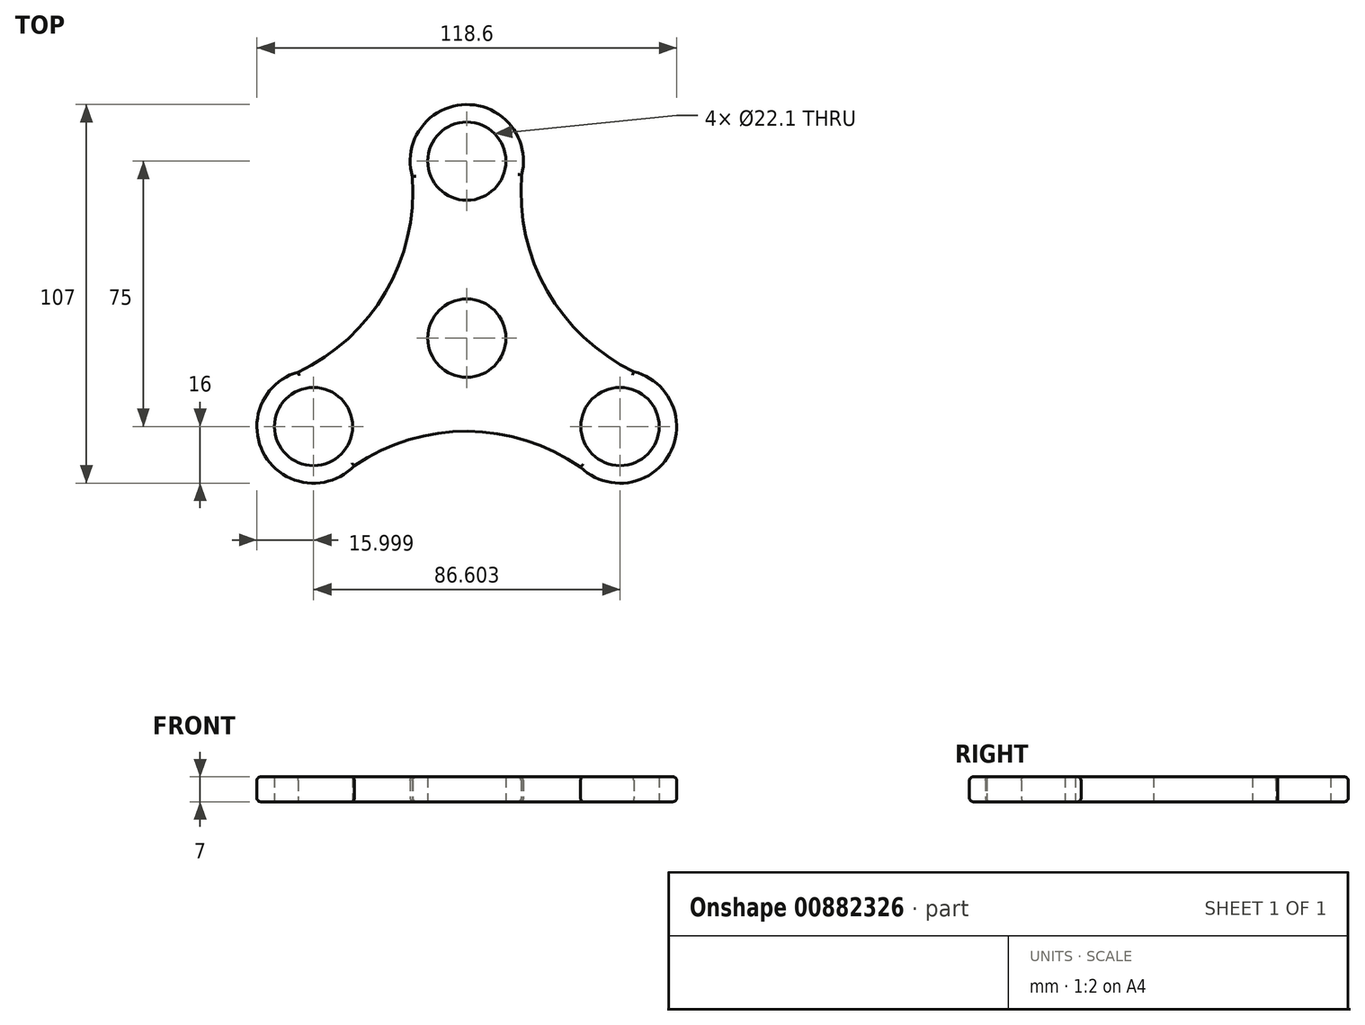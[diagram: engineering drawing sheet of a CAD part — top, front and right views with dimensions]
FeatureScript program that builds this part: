
annotation { "Feature Type Name" : "Feature", "Feature Type Description" : "" }
export const myFeature = defineFeature(function(context is Context, id is Id, definition is map)
    precondition{}
    {
        {
            var Q0;
            Q0=qCreatedBy(makeId("Top.planeOp"),FACE);
            var sketch = newSketch(context, id + "F0", { "sketchPlane" : qUnion([Q0])});
            skCircle(sketch, "E0", {"center": v(0, 0) * mm, "radius": 11.05 * mm});
            skCircle(sketch, "E1", {"center": v(0, 50) * mm, "radius": 11.05 * mm});
            skCircle(sketch, "E2.1.0", {"center": v(43.3, -25) * mm, "radius": 11.05 * mm});
            skCircle(sketch, "E2.2.0", {"center": v(-43.3, -25) * mm, "radius": 11.05 * mm});
            skLineSegment(sketch, "E2.anchor1", {"start": v(0, 0) * mm, "end": v(0, 50) * mm, "construction": true});
            skLineSegment(sketch, "E2.anchor2", {"start": v(0, 0) * mm, "end": v(-43.3, -25) * mm, "construction": true});
            skCircle(sketch, "E3", {"center": v(0, 50) * mm, "radius": 16 * mm});
            skCircle(sketch, "E4.1.0", {"center": v(-43.3, -25) * mm, "radius": 16 * mm});
            skCircle(sketch, "E4.2.0", {"center": v(43.3, -25) * mm, "radius": 16 * mm});
            skArc(sketch, "E5", {"start": v(15.52, 46.1) * mm, "mid": v(22.7, 13.38) * mm, "end": v(47.17, -9.48) * mm});
            skArc(sketch, "E6.1.0", {"start": v(-47.68, -9.6) * mm, "mid": v(-22.94, 12.96) * mm, "end": v(-15.38, 45.6) * mm});
            skArc(sketch, "E6.2.0", {"start": v(32.16, -36.48) * mm, "mid": v(0.24, -26.34) * mm, "end": v(-31.8, -36.12) * mm});
            skSolve(sketch);
        }
        {
            var Q0;
            Q0=makeQuery(id+"F0.imprint","IMPRINT",FACE,{"disambiguationData":[TD([[makeQuery(id+"F0.imprint","IMPRINT",EDGE,{"derivedFrom":sQuery(id+"F0.wireOp",EDGE,"E1")}),-1.0]])]});
            var Q1;
            Q1=makeQuery(id+"F0.imprint","IMPRINT",FACE,{"disambiguationData":[TD([[makeQuery(id+"F0.imprint","IMPRINT",EDGE,{"derivedFrom":sQuery(id+"F0.wireOp",EDGE,"E2.1.0")}),-1.0]])]});
            var Q2;
            Q2=makeQuery(id+"F0.imprint","IMPRINT",FACE,{"disambiguationData":[TD([[makeQuery(id+"F0.imprint","IMPRINT",EDGE,{"derivedFrom":sQuery(id+"F0.wireOp",EDGE,"E2.2.0")}),-1.0]])]});
            var Q3;
            Q3=makeQuery(id+"F0.imprint","IMPRINT",FACE,{"disambiguationData":[TD([[makeQuery(id+"F0.imprint","IMPRINT",EDGE,{"derivedFrom":sQuery(id+"F0.wireOp",EDGE,"E0")}),-1.0]])]});
            extrude(context, id + "F1", {"entities" : qUnion([Q0, Q1, Q2, Q3]), "depth" : 7 * mm, "offsetDistance" : 25 * mm});
        }
        {
            var Q0;
            Q0=makeQuery(id+"F1.opExtrude","CAP_EDGE",EDGE,{"disambiguationData":[OSD([sQuery(id+"F0.wireOp",EDGE,"E6.2.0")])],"isStart":false});
            var Q1;
            Q1=makeQuery(id+"F1.opExtrude","CAP_EDGE",EDGE,{"disambiguationData":[OSD([sQuery(id+"F0.wireOp",EDGE,"E4.2.0")])],"isStart":false});
            var Q2;
            Q2=makeQuery(id+"F1.opExtrude","CAP_EDGE",EDGE,{"disambiguationData":[OSD([sQuery(id+"F0.wireOp",EDGE,"E5")])],"isStart":false});
            var Q3;
            Q3=makeQuery(id+"F1.opExtrude","CAP_EDGE",EDGE,{"disambiguationData":[OSD([sQuery(id+"F0.wireOp",EDGE,"E3")])],"isStart":false});
            var Q4;
            Q4=makeQuery(id+"F1.opExtrude","CAP_EDGE",EDGE,{"disambiguationData":[OSD([sQuery(id+"F0.wireOp",EDGE,"E6.1.0")])],"isStart":false});
            var Q5;
            Q5=makeQuery(id+"F1.opExtrude","CAP_EDGE",EDGE,{"disambiguationData":[OSD([sQuery(id+"F0.wireOp",EDGE,"E4.1.0")])],"isStart":false});
            fillet(context, id + "F2", {"entities" : qUnion([Q0, Q1, Q2, Q3, Q4, Q5]), "radius" : 1 * mm, "tangentPropagation" : true, "allowEdgeOverflow" : false});
        }
        {
            var Q0;
            Q0=makeQuery(id+"F1.opExtrude","CAP_EDGE",EDGE,{"disambiguationData":[OSD([sQuery(id+"F0.wireOp",EDGE,"E6.2.0")])],"isStart":true});
            var Q1;
            Q1=makeQuery(id+"F1.opExtrude","CAP_EDGE",EDGE,{"disambiguationData":[OSD([sQuery(id+"F0.wireOp",EDGE,"E4.2.0")])],"isStart":true});
            var Q2;
            Q2=makeQuery(id+"F1.opExtrude","CAP_EDGE",EDGE,{"disambiguationData":[OSD([sQuery(id+"F0.wireOp",EDGE,"E5")])],"isStart":true});
            var Q3;
            Q3=makeQuery(id+"F1.opExtrude","CAP_EDGE",EDGE,{"disambiguationData":[OSD([sQuery(id+"F0.wireOp",EDGE,"E3")])],"isStart":true});
            var Q4;
            Q4=makeQuery(id+"F1.opExtrude","CAP_EDGE",EDGE,{"disambiguationData":[OSD([sQuery(id+"F0.wireOp",EDGE,"E6.1.0")])],"isStart":true});
            var Q5;
            Q5=makeQuery(id+"F1.opExtrude","CAP_EDGE",EDGE,{"disambiguationData":[OSD([sQuery(id+"F0.wireOp",EDGE,"E4.1.0")])],"isStart":true});
            fillet(context, id + "F3", {"entities" : qUnion([Q0, Q1, Q2, Q3, Q4, Q5]), "radius" : 1 * mm, "tangentPropagation" : true, "allowEdgeOverflow" : false});
        }
    });
